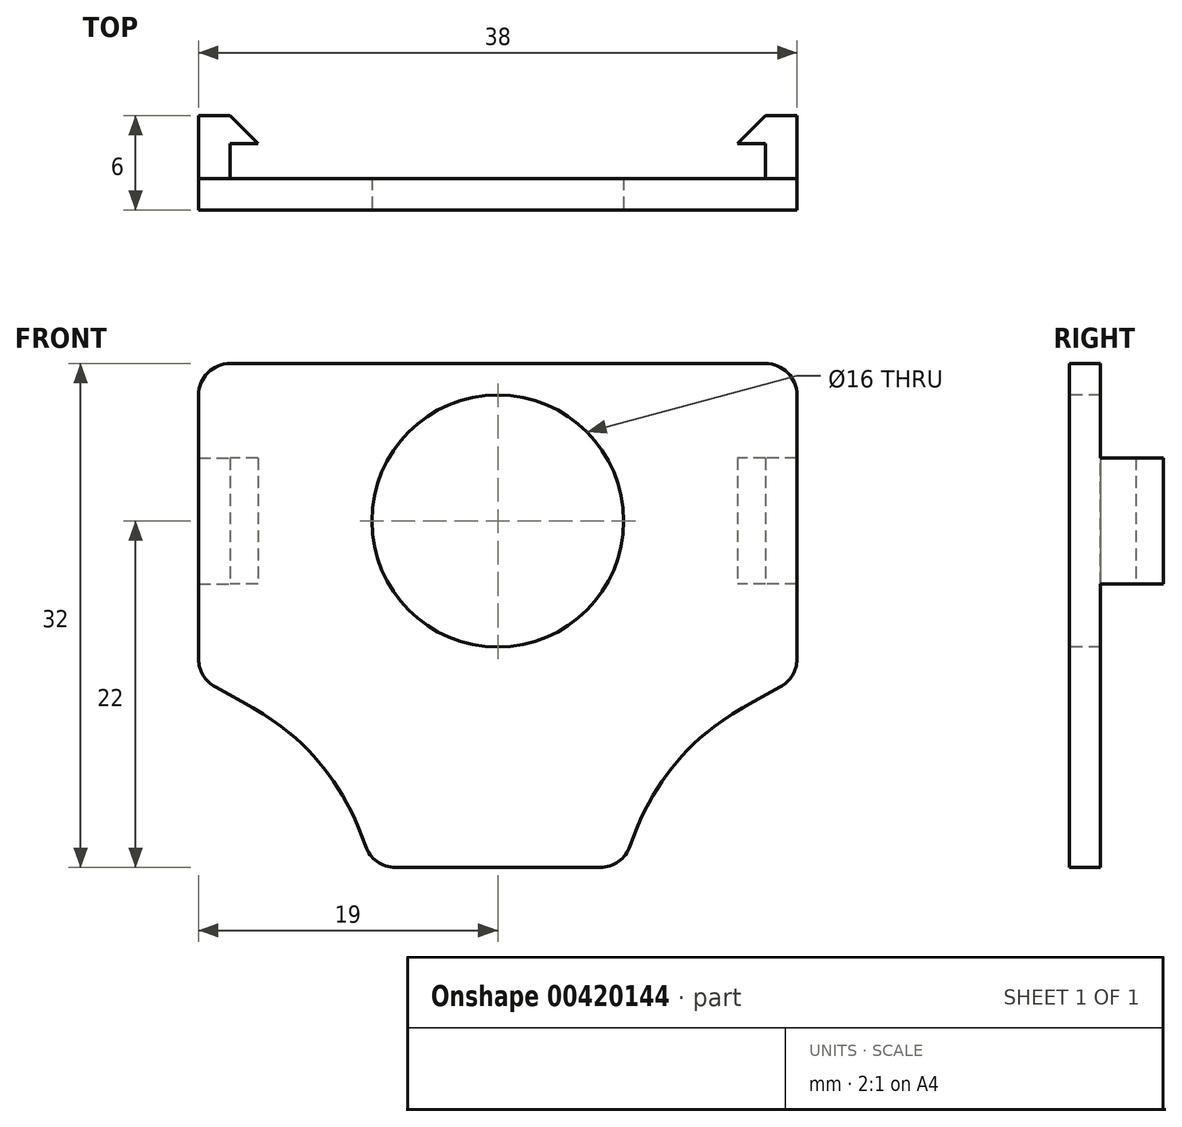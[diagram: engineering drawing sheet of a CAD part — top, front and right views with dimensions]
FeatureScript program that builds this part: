
annotation { "Feature Type Name" : "Feature", "Feature Type Description" : "" }
export const myFeature = defineFeature(function(context is Context, id is Id, definition is map)
    precondition{}
    {
        {
            var Q0;
            Q0=qCreatedBy(makeId("Front.planeOp"),FACE);
            var sketch = newSketch(context, id + "F0", { "sketchPlane" : qUnion([Q0])});
            skLineSegment(sketch, "E0.bottom", {"start": v(16.5, -14.5) * mm, "end": v(-16.5, -14.5) * mm, "construction": true});
            skLineSegment(sketch, "E0.top", {"start": v(16.5, 14.5) * mm, "end": v(-16.5, 14.5) * mm, "construction": true});
            skLineSegment(sketch, "E0.left", {"start": v(16.5, -14.5) * mm, "end": v(16.5, 14.5) * mm, "construction": true});
            skLineSegment(sketch, "E0.right", {"start": v(-16.5, -14.5) * mm, "end": v(-16.5, 14.5) * mm, "construction": true});
            skPoint(sketch, "E0.middle", {"position": v(0, 0) * mm});
            skLineSegment(sketch, "E1.bottom", {"start": v(19, -10) * mm, "end": v(-19, -10) * mm});
            skLineSegment(sketch, "E1.top", {"start": v(19, 10) * mm, "end": v(-19, 10) * mm});
            skLineSegment(sketch, "E1.left", {"start": v(19, -10) * mm, "end": v(19, 10) * mm});
            skLineSegment(sketch, "E1.right", {"start": v(-19, -10) * mm, "end": v(-19, 10) * mm});
            skLineSegment(sketch, "E2", {"start": v(0, 0) * mm, "end": v(0, -30.88) * mm, "construction": true});
            skLineSegment(sketch, "E3", {"start": v(0, -22) * mm, "end": v(-8, -22) * mm});
            skFitSpline(sketch, "E4", {"points": [v(-19, -10) * mm, v(-11, -15.77) * mm, v(-8, -22) * mm], "startDerivative": vector(26.52, -13.23) * mm, "endDerivative": vector(4.37, -17.19) * mm});
            skFitSpline(sketch, "E5.MirrorCS", {"points": [v(19, -10) * mm, v(11, -15.77) * mm, v(8, -22) * mm], "startDerivative": vector(-26.52, -13.23) * mm, "endDerivative": vector(-4.37, -17.19) * mm});
            skLineSegment(sketch, "E6.MirrorCS", {"start": v(0, -22) * mm, "end": v(8, -22) * mm});
            skSolve(sketch);
        }
        {
            var Q0;
            Q0 = qSketchRegion(id + "F0", true);
            extrude(context, id + "F1", {"entities" : qUnion([Q0]), "depth" : 2 * mm});
        }
        {
            var Q0;
            Q0=makeQuery(id+"F1.opExtrude","SWEPT_EDGE",EDGE,{"disambiguationData":[OSD([sQuery(id+"F0.wireOp",EDGE,"E1.top"),sQuery(id+"F0.wireOp",EDGE,"E1.right")])]});
            var Q1;
            Q1=makeQuery(id+"F1.opExtrude","SWEPT_EDGE",EDGE,{"disambiguationData":[OSD([sQuery(id+"F0.wireOp",EDGE,"E1.top"),sQuery(id+"F0.wireOp",EDGE,"E1.left")])]});
            var Q2;
            Q2=makeQuery(id+"F1.opExtrude","SWEPT_EDGE",EDGE,{"disambiguationData":[OSD([sQuery(id+"F0.wireOp",EDGE,"E3"),sQuery(id+"F0.wireOp",EDGE,"E4")])]});
            var Q3;
            Q3=makeQuery(id+"F1.opExtrude","SWEPT_EDGE",EDGE,{"disambiguationData":[OSD([sQuery(id+"F0.wireOp",EDGE,"E5.MirrorCS"),sQuery(id+"F0.wireOp",EDGE,"E6.MirrorCS")])]});
            var Q4;
            Q4=makeQuery(id+"F1.opExtrude","SWEPT_EDGE",EDGE,{"disambiguationData":[OSD([sQuery(id+"F0.wireOp",EDGE,"E1.bottom"),sQuery(id+"F0.wireOp",EDGE,"E1.right"),sQuery(id+"F0.wireOp",EDGE,"E4")])]});
            var Q5;
            Q5=makeQuery(id+"F1.opExtrude","SWEPT_EDGE",EDGE,{"disambiguationData":[OSD([sQuery(id+"F0.wireOp",EDGE,"E1.bottom"),sQuery(id+"F0.wireOp",EDGE,"E1.left"),sQuery(id+"F0.wireOp",EDGE,"E5.MirrorCS")])]});
            fillet(context, id + "F2", {"entities" : qUnion([Q0, Q1, Q2, Q3, Q4, Q5]), "radius" : 2 * mm, "tangentPropagation" : true, "allowEdgeOverflow" : false});
        }
        {
            var Q0;
            Q0=makeQuery(id+"F1.opExtrude","CAP_FACE",FACE,{"disambiguationData":[OSD([sQuery(id+"F0.wireOp",EDGE,"E1.top"),sQuery(id+"F0.wireOp",EDGE,"E1.left"),sQuery(id+"F0.wireOp",EDGE,"E1.right"),sQuery(id+"F0.wireOp",EDGE,"E3"),sQuery(id+"F0.wireOp",EDGE,"E4"),sQuery(id+"F0.wireOp",EDGE,"E5.MirrorCS"),sQuery(id+"F0.wireOp",EDGE,"E6.MirrorCS")])],"isStart":false});
            var sketch = newSketch(context, id + "F3", { "sketchPlane" : qUnion([Q0])});
            skCircle(sketch, "E7", {"center": v(0, 0) * mm, "radius": 8 * mm});
            skSolve(sketch);
        }
        {
            var Q0;
            Q0 = qSketchRegion(id + "F3", true);
            extrude(context, id + "F4", {"entities" : qUnion([Q0]), "operationType" : NewBodyOperationType.REMOVE, "endBound" : BoundingType.UP_TO_NEXT, "oppositeDirection" : true, "depth" : 25 * mm});
        }
        {
            var Q0;
            Q0=qCreatedBy(makeId("Top.planeOp"),FACE);
            var sketch = newSketch(context, id + "F5", { "sketchPlane" : qUnion([Q0])});
            skLineSegment(sketch, "E8.bottom", {"start": v(-19, 0) * mm, "end": v(-17, 0) * mm});
            skLineSegment(sketch, "E8.top", {"start": v(-19, 4) * mm, "end": v(-17, 4) * mm});
            skLineSegment(sketch, "E8.left", {"start": v(-19, 0) * mm, "end": v(-19, 4) * mm});
            skLineSegment(sketch, "E8.right", {"start": v(-17, 0) * mm, "end": v(-17, 2.23) * mm});
            skLineSegment(sketch, "E9", {"start": v(-17, 4) * mm, "end": v(-15.23, 2.23) * mm});
            skLineSegment(sketch, "E10", {"start": v(-15.23, 2.23) * mm, "end": v(-17, 2.23) * mm});
            skLineSegment(sketch, "E11", {"start": v(0, 0) * mm, "end": v(0, 9.4) * mm, "construction": true});
            skLineSegment(sketch, "E12.MirrorCS", {"start": v(19, 0) * mm, "end": v(17, 0) * mm});
            skLineSegment(sketch, "E13.MirrorCS", {"start": v(17, 0) * mm, "end": v(17, 2.23) * mm});
            skLineSegment(sketch, "E14.MirrorCS", {"start": v(15.23, 2.23) * mm, "end": v(17, 2.23) * mm});
            skLineSegment(sketch, "E15.MirrorCS", {"start": v(17, 4) * mm, "end": v(15.23, 2.23) * mm});
            skLineSegment(sketch, "E16.MirrorCS", {"start": v(19, 4) * mm, "end": v(17, 4) * mm});
            skLineSegment(sketch, "E17.MirrorCS", {"start": v(19, 0) * mm, "end": v(19, 4) * mm});
            skSolve(sketch);
        }
        {
            var Q0;
            Q0 = qSketchRegion(id + "F5", true);
            extrude(context, id + "F6", {"entities" : qUnion([Q0]), "operationType" : NewBodyOperationType.ADD, "depth" : 4 * mm, "hasSecondDirection" : true, "secondDirectionOppositeDirection" : true, "secondDirectionDepth" : 4 * mm});
        }
    });
